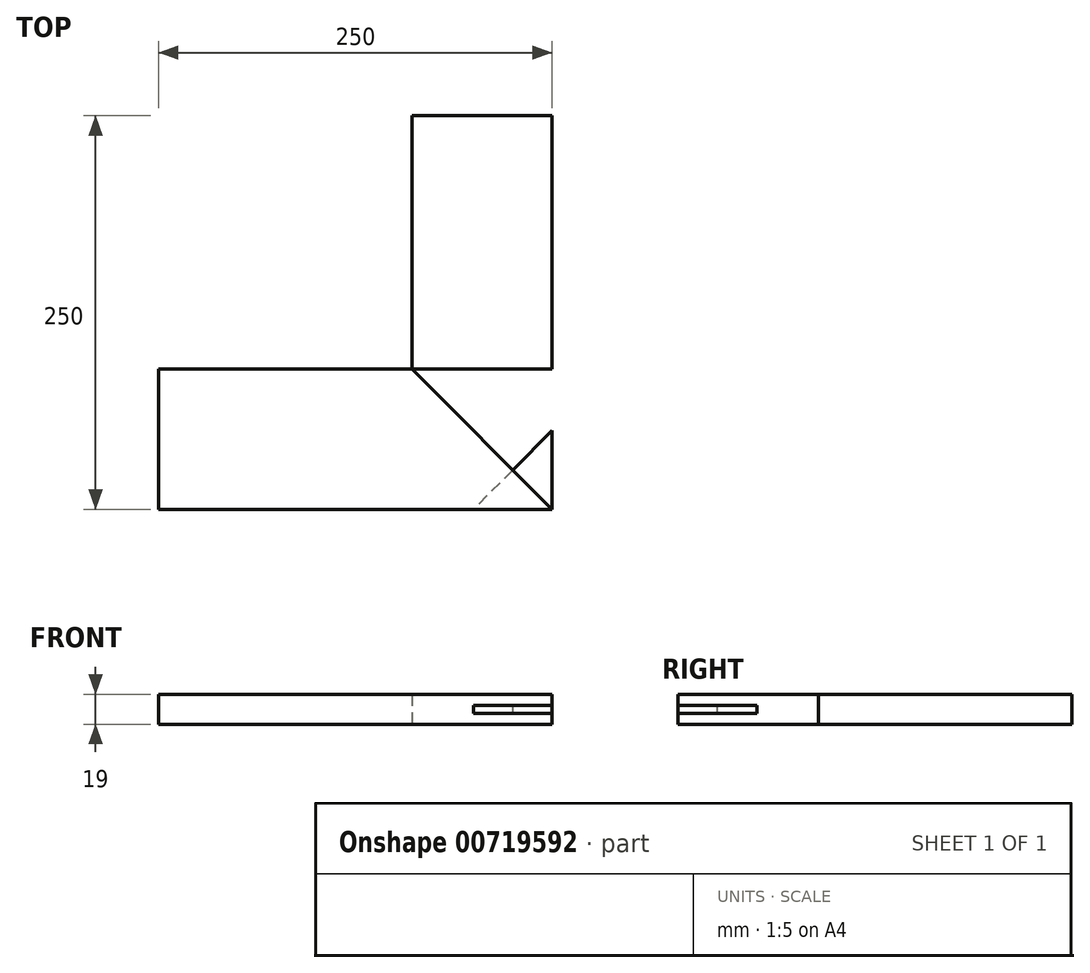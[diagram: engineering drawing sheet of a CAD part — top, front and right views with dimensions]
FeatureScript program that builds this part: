
annotation { "Feature Type Name" : "Feature", "Feature Type Description" : "" }
export const myFeature = defineFeature(function(context is Context, id is Id, definition is map)
    precondition{}
    {
        {
            var Q0;
            Q0=qCreatedBy(makeId("Top.planeOp"),FACE);
            var sketch = newSketch(context, id + "F0", { "sketchPlane" : qUnion([Q0])});
            skLineSegment(sketch, "E0.bottom", {"start": v(0, 0) * mm, "end": v(-250, 0) * mm});
            skLineSegment(sketch, "E0.top", {"start": v(0, 89) * mm, "end": v(-250, 89) * mm});
            skLineSegment(sketch, "E0.left", {"start": v(0, 89) * mm, "end": v(0, 0) * mm});
            skLineSegment(sketch, "E0.right", {"start": v(-250, 89) * mm, "end": v(-250, 0) * mm});
            skSolve(sketch);
        }
        {
            var Q0;
            Q0=makeQuery(id+"F0.imprint","IMPRINT",FACE,{"disambiguationData":[TD([[makeQuery(id+"F0.imprint","IMPRINT",EDGE,{"derivedFrom":sQuery(id+"F0.wireOp",EDGE,"E0.bottom")}),-1.0]])]});
            extrude(context, id + "F1", {"entities" : qUnion([Q0]), "depth" : 19 * mm, "offsetDistance" : 25 * mm});
        }
        {
            var Q0;
            Q0=qCreatedBy(makeId("Top.planeOp"),FACE);
            var sketch = newSketch(context, id + "F2", { "sketchPlane" : qUnion([Q0])});
            skLineSegment(sketch, "E1.bottom", {"start": v(0, 0) * mm, "end": v(-89, 0) * mm});
            skLineSegment(sketch, "E1.top", {"start": v(0, 250) * mm, "end": v(-89, 250) * mm});
            skLineSegment(sketch, "E1.left", {"start": v(0, 0) * mm, "end": v(0, 250) * mm});
            skLineSegment(sketch, "E1.right", {"start": v(-89, 0) * mm, "end": v(-89, 250) * mm});
            skSolve(sketch);
        }
        {
            var Q0;
            Q0=makeQuery(id+"F2.imprint","IMPRINT",FACE,{"disambiguationData":[TD([[makeQuery(id+"F2.imprint","IMPRINT",EDGE,{"derivedFrom":sQuery(id+"F2.wireOp",EDGE,"E1.bottom")}),-1.0]])]});
            extrude(context, id + "F3", {"entities" : qUnion([Q0]), "depth" : 19 * mm, "offsetDistance" : 25 * mm});
        }
        {
            var Q0;
            Q0=makeQuery(id+"F1.opExtrude","CAP_FACE",FACE,{"disambiguationData":[OSD([sQuery(id+"F0.wireOp",EDGE,"E0.bottom"),sQuery(id+"F0.wireOp",EDGE,"E0.top"),sQuery(id+"F0.wireOp",EDGE,"E0.left"),sQuery(id+"F0.wireOp",EDGE,"E0.right")])],"isStart":false});
            var sketch = newSketch(context, id + "F4", { "sketchPlane" : qUnion([Q0])});
            skLineSegment(sketch, "E2", {"start": v(0, 0) * mm, "end": v(-89, 89) * mm});
            skSolve(sketch);
        }
        {
            var Q0;
            {var subQ0=sQuery(id+"F4.wireOp",EDGE,"E2");Q0=makeQuery(id+"F4.imprint","IMPRINT",FACE,{"disambiguationData":[TD([[makeQuery(id+"F4.imprint","IMPRINT",EDGE,{"derivedFrom":subQ0}),-1.0]])]});}
            extrude(context, id + "F5", {"entities" : qUnion([Q0]), "operationType" : NewBodyOperationType.REMOVE, "endBound" : BoundingType.THROUGH_ALL, "oppositeDirection" : true, "depth" : 25 * mm, "offsetDistance" : 25 * mm});
        }
        {
            var Q0;
            Q0=makeQuery(id+"F1.opExtrude","SWEPT_BODY",BODY,{"disambiguationData":[OSD([sQuery(id+"F0.wireOp",EDGE,"E0.bottom"),sQuery(id+"F0.wireOp",EDGE,"E0.top"),sQuery(id+"F0.wireOp",EDGE,"E0.left"),sQuery(id+"F0.wireOp",EDGE,"E0.right")])]});
            var Q1;
            Q1=makeQuery(id+"F3.opExtrude","SWEPT_BODY",BODY,{"disambiguationData":[OSD([sQuery(id+"F2.wireOp",EDGE,"E1.bottom"),sQuery(id+"F2.wireOp",EDGE,"E1.top"),sQuery(id+"F2.wireOp",EDGE,"E1.left"),sQuery(id+"F2.wireOp",EDGE,"E1.right")])]});
            booleanBodies(context, id + "F6", {"operationType" : BooleanOperationType.SUBTRACTION, "tools" : qUnion([Q0]), "targets" : qUnion([Q1]), "keepTools" : true});
        }
        {
            var Q0;
            Q0=makeQuery(id+"F1.opExtrude","CAP_FACE",FACE,{"disambiguationData":[OSD([sQuery(id+"F0.wireOp",EDGE,"E0.bottom"),sQuery(id+"F0.wireOp",EDGE,"E0.top"),sQuery(id+"F0.wireOp",EDGE,"E0.left"),sQuery(id+"F0.wireOp",EDGE,"E0.right")])],"isStart":true});
            var Q1;
            Q1=makeQuery(id+"F1.opExtrude","CAP_FACE",FACE,{"disambiguationData":[OSD([sQuery(id+"F0.wireOp",EDGE,"E0.bottom"),sQuery(id+"F0.wireOp",EDGE,"E0.top"),sQuery(id+"F0.wireOp",EDGE,"E0.left"),sQuery(id+"F0.wireOp",EDGE,"E0.right")])],"isStart":false});
            cPlane(context, id + "F7", {"entities" : qUnion([Q0, Q1]), "cplaneType" : CPlaneType.MID_PLANE, "offset" : 25 * mm, "width" : 150 * mm, "height" : 150 * mm});
        }
        {
            var Q0;
            Q0=qCreatedBy(id+"F7.planeOp",FACE);
            var sketch = newSketch(context, id + "F8", { "sketchPlane" : qUnion([Q0])});
            skLineSegment(sketch, "E3", {"start": v(0, -50) * mm, "end": v(-50, 0) * mm});
            skLineSegment(sketch, "E4.0", {"start": v(0, 0) * mm, "end": v(-250, 0) * mm});
            skLineSegment(sketch, "E5.0", {"start": v(0, 0) * mm, "end": v(0, -250) * mm});
            skSolve(sketch);
        }
        {
            var Q0;
            Q0 = qSketchRegion(id + "F8", true);
            extrude(context, id + "F9", {"entities" : qUnion([Q0]), "endBound" : BoundingType.SYMMETRIC, "depth" : 5 * mm, "offsetDistance" : 25 * mm});
        }
        {
            var Q0;
            Q0=makeQuery(id+"F9.opExtrude","SWEPT_BODY",BODY,{"disambiguationData":[OSD([sQuery(id+"F8.wireOp",EDGE,"E3"),sQuery(id+"F8.wireOp",EDGE,"E4.0"),sQuery(id+"F8.wireOp",EDGE,"E5.0")])]});
            var Q1;
            Q1=makeQuery(id+"F1.opExtrude","SWEPT_BODY",BODY,{"disambiguationData":[OSD([sQuery(id+"F0.wireOp",EDGE,"E0.bottom"),sQuery(id+"F0.wireOp",EDGE,"E0.top"),sQuery(id+"F0.wireOp",EDGE,"E0.left"),sQuery(id+"F0.wireOp",EDGE,"E0.right")])]});
            var Q2;
            Q2=makeQuery(id+"F3.opExtrude","SWEPT_BODY",BODY,{"disambiguationData":[OSD([sQuery(id+"F2.wireOp",EDGE,"E1.bottom"),sQuery(id+"F2.wireOp",EDGE,"E1.top"),sQuery(id+"F2.wireOp",EDGE,"E1.left"),sQuery(id+"F2.wireOp",EDGE,"E1.right")])]});
            booleanBodies(context, id + "F10", {"operationType" : BooleanOperationType.SUBTRACTION, "tools" : qUnion([Q0]), "targets" : qUnion([Q1, Q2]), "keepTools" : true});
        }
    });
